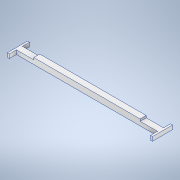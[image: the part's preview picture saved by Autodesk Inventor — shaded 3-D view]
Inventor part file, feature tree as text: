
AUTODESK INVENTOR PART (.ipt)
format: ipt  version: 2020.1 (Build 241239000, 239)  size: 133,632 bytes
history: native  units: mm
features: extrude x2, sketch x2, other x1
ambient origin geometry x8: Origin, YZ Plane, XZ Plane, XY Plane, X Axis, Y Axis, Z Axis, Center Point
bodies: Body1 (feature_tree)
feature tree (5):
  other  "Твердое тело1"
  extrude  "Выдавливание1"  Depth=30.0mm
  extrude  "Выдавливание2"  Depth=100.0mm
  sketch  "Эскиз1"
  sketch  "Эскиз2"
